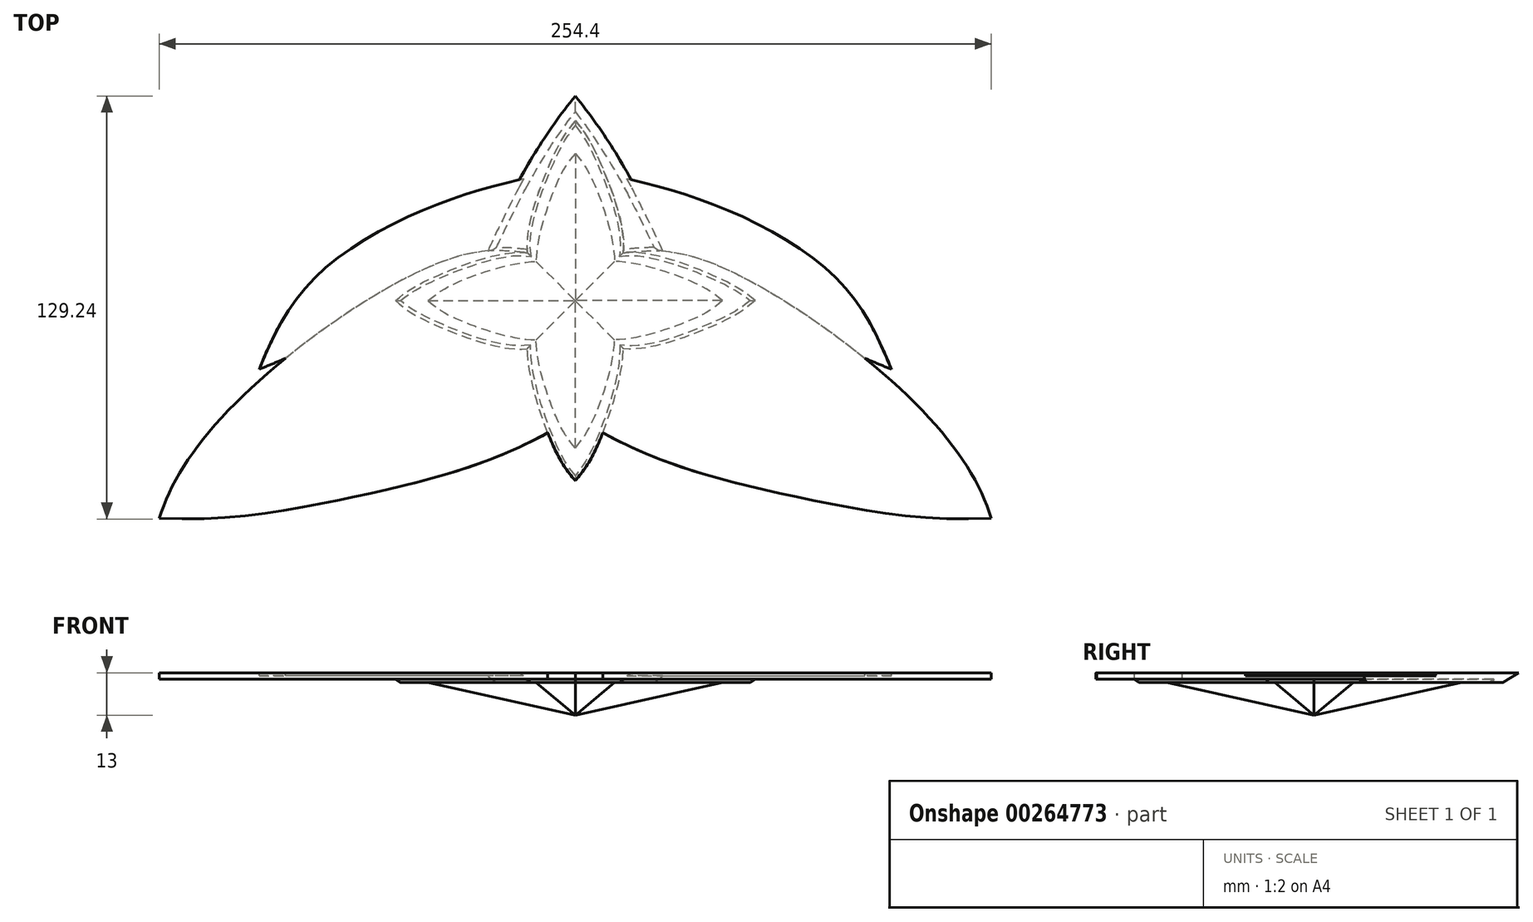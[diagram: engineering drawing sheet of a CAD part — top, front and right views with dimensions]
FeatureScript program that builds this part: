
annotation { "Feature Type Name" : "Feature", "Feature Type Description" : "" }
export const myFeature = defineFeature(function(context is Context, id is Id, definition is map)
    precondition{}
    {
        {
            var Q0;
            Q0=qCreatedBy(makeId("Top.planeOp"),FACE);
            var sketch = newSketch(context, id + "F0", { "sketchPlane" : qUnion([Q0])});
            skLineSegment(sketch, "E0", {"start": v(0, 0) * mm, "end": v(0, 50) * mm});
            skLineSegment(sketch, "E1", {"start": v(0, 0) * mm, "end": v(-50, 0) * mm});
            skFitSpline(sketch, "E2", {"points": [v(0, 50) * mm, v(-50, 0) * mm], "startDerivative": vector(-22.26, -93.04) * mm, "endDerivative": vector(-77.74, -6.96) * mm});
            skFitSpline(sketch, "E3.MirrorCS", {"points": [v(0, 50) * mm, v(50, 0) * mm], "startDerivative": vector(22.26, -93.04) * mm, "endDerivative": vector(77.74, -6.96) * mm});
            skFitSpline(sketch, "E4.MirrorCS", {"points": [v(0, -50) * mm, v(-50, 0) * mm], "startDerivative": vector(-22.26, 93.04) * mm, "endDerivative": vector(-77.74, 6.96) * mm});
            skFitSpline(sketch, "E5.MirrorCS", {"points": [v(0, -50) * mm, v(50, 0) * mm], "startDerivative": vector(22.26, 93.04) * mm, "endDerivative": vector(77.74, 6.96) * mm});
            skSolve(sketch);
        }
        {
            var Q0;
            Q0=qCreatedBy(makeId("Top.planeOp"),FACE);
            var sketch = newSketch(context, id + "F1", { "sketchPlane" : qUnion([Q0])});
            skFitSpline(sketch, "E6", {"points": [v(0, 49.98) * mm, v(-7.34, 30.13) * mm, v(-11.2, 11.2) * mm], "startDerivative": vector(-14.95, -18.4) * mm, "endDerivative": vector(-4.03, -50.51) * mm});
            skFitSpline(sketch, "E7.MirrorCS", {"points": [v(0, 49.98) * mm, v(7.34, 30.13) * mm, v(11.2, 11.2) * mm], "startDerivative": vector(14.95, -18.4) * mm, "endDerivative": vector(4.03, -50.51) * mm});
            skFitSpline(sketch, "E8.MirrorCS", {"points": [v(0, -49.98) * mm, v(-7.34, -30.13) * mm, v(-11.2, -11.2) * mm], "startDerivative": vector(-14.95, 18.4) * mm, "endDerivative": vector(-4.03, 50.51) * mm});
            skFitSpline(sketch, "E9.MirrorCS", {"points": [v(0, -49.98) * mm, v(7.34, -30.13) * mm, v(11.2, -11.2) * mm], "startDerivative": vector(14.95, 18.4) * mm, "endDerivative": vector(4.03, 50.51) * mm});
            skLineSegment(sketch, "E10", {"start": v(-11.2, 11.2) * mm, "end": v(11.2, -11.2) * mm, "construction": true});
            skLineSegment(sketch, "E11", {"start": v(11.2, 11.2) * mm, "end": v(-11.2, -11.2) * mm, "construction": true});
            skFitSpline(sketch, "E12.MirrorCS", {"points": [v(-49.98, 0) * mm, v(-30.13, -7.34) * mm, v(-11.2, -11.2) * mm], "startDerivative": vector(18.4, -14.95) * mm, "endDerivative": vector(50.51, -4.03) * mm});
            skFitSpline(sketch, "E13.MirrorCS", {"points": [v(-49.98, 0) * mm, v(-30.13, 7.34) * mm, v(-11.2, 11.2) * mm], "startDerivative": vector(18.4, 14.95) * mm, "endDerivative": vector(50.51, 4.03) * mm});
            skFitSpline(sketch, "E14.MirrorCS", {"points": [v(49.98, 0) * mm, v(30.13, 7.34) * mm, v(11.2, 11.2) * mm], "startDerivative": vector(-18.4, 14.95) * mm, "endDerivative": vector(-50.51, 4.03) * mm});
            skFitSpline(sketch, "E15.MirrorCS", {"points": [v(49.98, 0) * mm, v(30.13, -7.34) * mm, v(11.2, -11.2) * mm], "startDerivative": vector(-18.4, -14.95) * mm, "endDerivative": vector(-50.51, -4.03) * mm});
            skLineSegment(sketch, "E16", {"start": v(0, 49.98) * mm, "end": v(0, 0) * mm, "construction": true});
            skLineSegment(sketch, "E17", {"start": v(0, 0) * mm, "end": v(0, -49.98) * mm, "construction": true});
            skLineSegment(sketch, "E18", {"start": v(0, 0) * mm, "end": v(49.98, 0) * mm, "construction": true});
            skLineSegment(sketch, "E19", {"start": v(0, 0) * mm, "end": v(-49.98, 0) * mm, "construction": true});
            skSolve(sketch);
        }
        {
            var Q0;
            Q0=qCreatedBy(makeId("Top.planeOp"),FACE);
            cPlane(context, id + "F2", {"entities" : qUnion([Q0]), "cplaneType" : CPlaneType.OFFSET, "offset" : 10 * mm, "width" : 150 * mm, "height" : 150 * mm});
        }
        {
            var Q0;
            Q0=qCreatedBy(id+"F2.planeOp",FACE);
            var sketch = newSketch(context, id + "F3", { "sketchPlane" : qUnion([Q0])});
            skLineSegment(sketch, "E20", {"start": v(0, 0) * mm, "end": v(0, 45) * mm, "construction": true});
            skFitSpline(sketch, "E21", {"points": [v(0, 45) * mm, v(-6.46, 34.06) * mm, v(-11.98, 11.98) * mm], "startDerivative": vector(-19.81, -22.58) * mm, "endDerivative": vector(-0.12, -34.14) * mm});
            skFitSpline(sketch, "E22.MirrorCS", {"points": [v(0, 45) * mm, v(6.46, 34.06) * mm, v(11.98, 11.98) * mm], "startDerivative": vector(19.81, -22.58) * mm, "endDerivative": vector(0.12, -34.14) * mm});
            skFitSpline(sketch, "E23.MirrorCS", {"points": [v(0, -45) * mm, v(-6.46, -34.06) * mm, v(-11.98, -11.98) * mm], "startDerivative": vector(-19.81, 22.58) * mm, "endDerivative": vector(-0.12, 34.14) * mm});
            skFitSpline(sketch, "E24.MirrorCS", {"points": [v(0, -45) * mm, v(6.46, -34.06) * mm, v(11.98, -11.98) * mm], "startDerivative": vector(19.81, 22.58) * mm, "endDerivative": vector(0.12, 34.14) * mm});
            skLineSegment(sketch, "E25", {"start": v(-11.98, 11.98) * mm, "end": v(11.98, -11.98) * mm, "construction": true});
            skLineSegment(sketch, "E26", {"start": v(11.98, 11.98) * mm, "end": v(-11.98, -11.98) * mm, "construction": true});
            skFitSpline(sketch, "E27.MirrorCS", {"points": [v(-45, 0) * mm, v(-34.06, 6.46) * mm, v(-11.98, 11.98) * mm], "startDerivative": vector(22.58, 19.81) * mm, "endDerivative": vector(34.14, 0.12) * mm});
            skFitSpline(sketch, "E28.MirrorCS", {"points": [v(-45, 0) * mm, v(-34.06, -6.46) * mm, v(-11.98, -11.98) * mm], "startDerivative": vector(22.58, -19.81) * mm, "endDerivative": vector(34.14, -0.12) * mm});
            skFitSpline(sketch, "E29.MirrorCS", {"points": [v(45, 0) * mm, v(34.06, -6.46) * mm, v(11.98, -11.98) * mm], "startDerivative": vector(-22.58, -19.81) * mm, "endDerivative": vector(-34.14, -0.12) * mm});
            skFitSpline(sketch, "E30.MirrorCS", {"points": [v(45, 0) * mm, v(34.06, 6.46) * mm, v(11.98, 11.98) * mm], "startDerivative": vector(-22.58, 19.81) * mm, "endDerivative": vector(-34.14, 0.12) * mm});
            skLineSegment(sketch, "E31", {"start": v(0, -45) * mm, "end": v(0, 45) * mm, "construction": true});
            skSolve(sketch);
        }
        {
            var Q0;
            Q0=makeQuery(id+"F3.imprint","IMPRINT",FACE,{"disambiguationData":[TD([[makeQuery(id+"F3.imprint","IMPRINT",EDGE,{"derivedFrom":sQuery(id+"F3.wireOp",EDGE,"E21")}),1.0]])]});
            var Q1;
            Q1=qCreatedBy(makeId("Origin.pointOp"),VERTEX);
            loft(context, id + "F4", {"sheetProfilesArray" : [{ "sheetProfileEntities" : qUnion([Q0]) }, { "sheetProfileEntities" : qUnion([Q1]) }]});
        }
        {
            var Q0;
            Q0=makeQuery(id+"F4.opLoft","CAP_FACE",FACE,{"disambiguationData":[OSD([makeQuery(id+"F3.imprint","IMPRINT",FACE,{"disambiguationData":[TD([[makeQuery(id+"F3.imprint","IMPRINT",EDGE,{"derivedFrom":sQuery(id+"F3.wireOp",EDGE,"E21")}),1.0]])]})])],"isStart":true});
            var sketch = newSketch(context, id + "F5", { "sketchPlane" : qUnion([Q0])});
            skLineSegment(sketch, "E32", {"start": v(0, 0) * mm, "end": v(0, 55) * mm, "construction": true});
            skFitSpline(sketch, "E33", {"points": [v(0, 55) * mm, v(-7.9, 41.63) * mm, v(-14.64, 14.64) * mm], "startDerivative": vector(-24.22, -27.6) * mm, "endDerivative": vector(5.42, -38.74) * mm});
            skFitSpline(sketch, "E34.MirrorCS", {"points": [v(0, 55) * mm, v(7.9, 41.63) * mm, v(14.64, 14.64) * mm], "startDerivative": vector(24.22, -27.6) * mm, "endDerivative": vector(-5.42, -38.74) * mm});
            skFitSpline(sketch, "E35.MirrorCS", {"points": [v(0, -55) * mm, v(-7.9, -41.63) * mm, v(-14.64, -14.64) * mm], "startDerivative": vector(-24.22, 27.6) * mm, "endDerivative": vector(-0.14, 41.73) * mm});
            skFitSpline(sketch, "E36.MirrorCS", {"points": [v(0, -55) * mm, v(7.9, -41.63) * mm, v(14.64, -14.64) * mm], "startDerivative": vector(24.22, 27.6) * mm, "endDerivative": vector(0.14, 41.73) * mm});
            skLineSegment(sketch, "E37", {"start": v(-14.64, 14.64) * mm, "end": v(14.64, -14.64) * mm, "construction": true});
            skLineSegment(sketch, "E38", {"start": v(14.64, 14.64) * mm, "end": v(-14.64, -14.64) * mm, "construction": true});
            skFitSpline(sketch, "E39.MirrorCS", {"points": [v(-55, 0) * mm, v(-41.63, 7.9) * mm, v(-14.64, 14.64) * mm], "startDerivative": vector(27.6, 24.22) * mm, "endDerivative": vector(38.74, -5.42) * mm});
            skFitSpline(sketch, "E40.MirrorCS", {"points": [v(-55, 0) * mm, v(-41.63, -7.9) * mm, v(-14.64, -14.64) * mm], "startDerivative": vector(27.6, -24.22) * mm, "endDerivative": vector(38.74, 5.42) * mm});
            skFitSpline(sketch, "E41.MirrorCS", {"points": [v(55, 0) * mm, v(41.63, -7.9) * mm, v(14.64, -14.64) * mm], "startDerivative": vector(-27.6, -24.22) * mm, "endDerivative": vector(-38.74, 5.42) * mm});
            skFitSpline(sketch, "E42.MirrorCS", {"points": [v(55, 0) * mm, v(41.63, 7.9) * mm, v(14.64, 14.64) * mm], "startDerivative": vector(-27.6, 24.22) * mm, "endDerivative": vector(-38.74, -5.42) * mm});
            skLineSegment(sketch, "E43", {"start": v(0, -55) * mm, "end": v(0, 0) * mm, "construction": true});
            skLineSegment(sketch, "E44", {"start": v(55, 0) * mm, "end": v(0, 0) * mm, "construction": true});
            skLineSegment(sketch, "E45", {"start": v(0, 55) * mm, "end": v(0, 0) * mm, "construction": true});
            skLineSegment(sketch, "E46", {"start": v(0, 0) * mm, "end": v(-55, 0) * mm, "construction": true});
            skSolve(sketch);
        }
        {
            var Q0;
            Q0=makeQuery(id+"F5.imprint","IMPRINT",FACE,{"disambiguationData":[TD([[makeQuery(id+"F5.imprint","IMPRINT",EDGE,{"derivedFrom":sQuery(id+"F5.wireOp",EDGE,"E33")}),1.0]])]});
            var Q1;
            {var subQ2=sQuery(id+"F3.wireOp",EDGE,"E22.MirrorCS");var subQ4=sQuery(id+"F3.wireOp",EDGE,"E27.MirrorCS");var subQ5=sQuery(id+"F3.wireOp",EDGE,"E21");Q1=makeQuery(id+"F5.imprint","IMPRINT",FACE,{"disambiguationData":[TD([[makeQuery(id+"F5.imprint","IMPRINT",EDGE,{"derivedFrom":makeQuery(id+"F4.opLoft","MID_CAP_EDGE",EDGE,{"disambiguationData":[OSD([subQ5,subQ2,subQ4])],"capPos":0.0})}),1.0]])]});}
            extrude(context, id + "F6", {"entities" : qUnion([Q0, Q1]), "operationType" : NewBodyOperationType.ADD, "depth" : 3 * mm, "offsetDistance" : 25 * mm});
        }
        {
            var Q0;
            Q0=makeQuery(id+"F6.opExtrude","CAP_EDGE",EDGE,{"disambiguationData":[OSD([sQuery(id+"F5.wireOp",EDGE,"E35.MirrorCS")])],"isStart":true});
            var Q1;
            Q1=makeQuery(id+"F6.opExtrude","CAP_EDGE",EDGE,{"disambiguationData":[OSD([sQuery(id+"F5.wireOp",EDGE,"E36.MirrorCS")])],"isStart":true});
            var Q2;
            Q2=makeQuery(id+"F6.opExtrude","CAP_EDGE",EDGE,{"disambiguationData":[OSD([sQuery(id+"F5.wireOp",EDGE,"E40.MirrorCS")])],"isStart":true});
            var Q3;
            Q3=makeQuery(id+"F6.opExtrude","CAP_EDGE",EDGE,{"disambiguationData":[OSD([sQuery(id+"F5.wireOp",EDGE,"E39.MirrorCS")])],"isStart":true});
            var Q4;
            Q4=makeQuery(id+"F6.opExtrude","CAP_EDGE",EDGE,{"disambiguationData":[OSD([sQuery(id+"F5.wireOp",EDGE,"E33")])],"isStart":true});
            var Q5;
            Q5=makeQuery(id+"F6.opExtrude","CAP_EDGE",EDGE,{"disambiguationData":[OSD([sQuery(id+"F5.wireOp",EDGE,"E34.MirrorCS")])],"isStart":true});
            var Q6;
            Q6=makeQuery(id+"F6.opExtrude","CAP_EDGE",EDGE,{"disambiguationData":[OSD([sQuery(id+"F5.wireOp",EDGE,"E42.MirrorCS")])],"isStart":true});
            var Q7;
            Q7=makeQuery(id+"F6.opExtrude","CAP_EDGE",EDGE,{"disambiguationData":[OSD([sQuery(id+"F5.wireOp",EDGE,"E41.MirrorCS")])],"isStart":true});
            chamfer(context, id + "F7", {"entities" : qUnion([Q0, Q1, Q2, Q3, Q4, Q5, Q6, Q7]), "width" : 1 * mm, "tangentPropagation" : true});
        }
        {
            var Q0;
            Q0=makeQuery(id+"F6.opExtrude","CAP_FACE",FACE,{"disambiguationData":[OSD([sQuery(id+"F5.wireOp",EDGE,"E33"),sQuery(id+"F5.wireOp",EDGE,"E34.MirrorCS"),sQuery(id+"F5.wireOp",EDGE,"E35.MirrorCS"),sQuery(id+"F5.wireOp",EDGE,"E36.MirrorCS"),sQuery(id+"F5.wireOp",EDGE,"E39.MirrorCS"),sQuery(id+"F5.wireOp",EDGE,"E40.MirrorCS"),sQuery(id+"F5.wireOp",EDGE,"E41.MirrorCS"),sQuery(id+"F5.wireOp",EDGE,"E42.MirrorCS")])],"isStart":false});
            var sketch = newSketch(context, id + "F8", { "sketchPlane" : qUnion([Q0])});
            skFitSpline(sketch, "E47", {"points": [v(8.4, -40.37) * mm, v(38.63, -52.8) * mm, v(73.35, -61.15) * mm, v(127.2, -66.45) * mm], "startDerivative": vector(101.37, -54.96) * mm, "endDerivative": vector(163.5, 9.13) * mm});
            skFitSpline(sketch, "E48", {"points": [v(14.64, 14.64) * mm, v(38.6, 12.68) * mm, v(102.88, -30.26) * mm, v(127.2, -66.45) * mm], "startDerivative": vector(85.37, 9.14) * mm, "endDerivative": vector(31.49, -101.03) * mm});
            skFitSpline(sketch, "E49", {"points": [v(9.14, 38.67) * mm, v(42.23, 29.41) * mm, v(80.3, 6.36) * mm, v(96.65, -20.99) * mm], "startDerivative": vector(93.7, -19.67) * mm, "endDerivative": vector(36.32, -89.57) * mm});
            skFitSpline(sketch, "E50", {"points": [v(96.65, -20.99) * mm, v(88.57, -17.6) * mm], "startDerivative": vector(-8.1, 3.36) * mm, "endDerivative": vector(-8.1, 3.36) * mm});
            skFitSpline(sketch, "E51.MirrorCS", {"points": [v(-8.4, -40.37) * mm, v(-38.63, -52.8) * mm, v(-73.35, -61.15) * mm, v(-127.2, -66.45) * mm], "startDerivative": vector(-101.37, -54.96) * mm, "endDerivative": vector(-163.5, 9.13) * mm});
            skFitSpline(sketch, "E52.MirrorCS", {"points": [v(-14.64, 14.64) * mm, v(-38.6, 12.68) * mm, v(-102.88, -30.26) * mm, v(-127.2, -66.45) * mm], "startDerivative": vector(-85.37, 9.14) * mm, "endDerivative": vector(-31.49, -101.03) * mm});
            skFitSpline(sketch, "E53.MirrorCS", {"points": [v(-9.14, 38.67) * mm, v(-42.23, 29.41) * mm, v(-80.3, 6.36) * mm, v(-96.65, -20.99) * mm], "startDerivative": vector(-93.7, -19.67) * mm, "endDerivative": vector(-36.32, -89.57) * mm});
            skFitSpline(sketch, "E54.MirrorCS", {"points": [v(-96.65, -20.99) * mm, v(-88.57, -17.6) * mm], "startDerivative": vector(8.1, 3.36) * mm, "endDerivative": vector(8.1, 3.36) * mm});
            skFitSpline(sketch, "E55", {"points": [v(-31.44, 11.84) * mm, v(-25.1, 25.7) * mm, v(0, 65.66) * mm], "startDerivative": vector(13.55, 33.83) * mm, "endDerivative": vector(59.2, 69.46) * mm});
            skFitSpline(sketch, "E56.MirrorCS", {"points": [v(31.44, 11.84) * mm, v(25.1, 25.7) * mm, v(0, 65.66) * mm], "startDerivative": vector(-13.55, 33.83) * mm, "endDerivative": vector(-59.2, 69.46) * mm});
            skSolve(sketch);
        }
        {
            var Q0;
            {var subQ4=sQuery(id+"F8.wireOp",EDGE,"E51.MirrorCS");Q0=makeQuery(id+"F8.imprint","IMPRINT",FACE,{"disambiguationData":[TD([[makeQuery(id+"F8.imprint","IMPRINT",EDGE,{"derivedFrom":subQ4}),-1.0]])]});}
            var Q1;
            {var subQ5=sQuery(id+"F8.wireOp",EDGE,"E47");Q1=makeQuery(id+"F8.imprint","IMPRINT",FACE,{"disambiguationData":[TD([[makeQuery(id+"F8.imprint","IMPRINT",EDGE,{"derivedFrom":subQ5}),1.0]])]});}
            var Q2;
            {var subQ0=sQuery(id+"F8.wireOp",EDGE,"E55");var subQ1=sQuery(id+"F8.wireOp",EDGE,"E52.MirrorCS");var subQ2=makeQuery(id+"F8.imprint","INTERSECT",VERTEX,{"derivedFrom":[subQ1,subQ0]});Q2=makeQuery(id+"F8.imprint","IMPRINT",FACE,{"disambiguationData":[TD([[makeQuery(id+"F8.imprint","IMPRINT",EDGE,{"disambiguationData":[TD([[subQ2,1.0]])],"derivedFrom":subQ1}),1.0]])]});}
            var Q3;
            {var subQ0=sQuery(id+"F8.wireOp",EDGE,"E56.MirrorCS");var subQ1=sQuery(id+"F8.wireOp",EDGE,"E48");var subQ2=makeQuery(id+"F8.imprint","INTERSECT",VERTEX,{"derivedFrom":[subQ1,subQ0]});Q3=makeQuery(id+"F8.imprint","IMPRINT",FACE,{"disambiguationData":[TD([[makeQuery(id+"F8.imprint","IMPRINT",EDGE,{"disambiguationData":[TD([[subQ2,1.0]])],"derivedFrom":subQ1}),-1.0]])]});}
            extrude(context, id + "F9", {"entities" : qUnion([Q0, Q1, Q2, Q3]), "operationType" : NewBodyOperationType.ADD, "oppositeDirection" : true, "depth" : 2 * mm, "offsetDistance" : 25 * mm});
        }
        {
            var Q0;
            {var subQ6=sQuery(id+"F8.wireOp",EDGE,"E53.MirrorCS");Q0=makeQuery(id+"F8.imprint","IMPRINT",FACE,{"disambiguationData":[TD([[makeQuery(id+"F8.imprint","IMPRINT",EDGE,{"derivedFrom":subQ6}),1.0]])]});}
            var Q1;
            {var subQ1=sQuery(id+"F8.wireOp",EDGE,"E49");Q1=makeQuery(id+"F8.imprint","IMPRINT",FACE,{"disambiguationData":[TD([[makeQuery(id+"F8.imprint","IMPRINT",EDGE,{"derivedFrom":subQ1}),-1.0]])]});}
            var Q2;
            {var subQ0=sQuery(id+"F8.wireOp",EDGE,"E55");var subQ3=sQuery(id+"F8.wireOp",EDGE,"E52.MirrorCS");var subQ4=makeQuery(id+"F8.imprint","INTERSECT",VERTEX,{"derivedFrom":[subQ3,subQ0]});Q2=makeQuery(id+"F8.imprint","IMPRINT",FACE,{"disambiguationData":[TD([[makeQuery(id+"F8.imprint","IMPRINT",EDGE,{"disambiguationData":[TD([[subQ4,1.0]])],"derivedFrom":subQ3}),-1.0]])]});}
            var Q3;
            {var subQ0=sQuery(id+"F8.wireOp",EDGE,"E56.MirrorCS");var subQ3=sQuery(id+"F8.wireOp",EDGE,"E48");var subQ4=makeQuery(id+"F8.imprint","INTERSECT",VERTEX,{"derivedFrom":[subQ3,subQ0]});Q3=makeQuery(id+"F8.imprint","IMPRINT",FACE,{"disambiguationData":[TD([[makeQuery(id+"F8.imprint","IMPRINT",EDGE,{"disambiguationData":[TD([[subQ4,1.0]])],"derivedFrom":subQ3}),1.0]])]});}
            extrude(context, id + "F10", {"entities" : qUnion([Q0, Q1, Q2, Q3]), "operationType" : NewBodyOperationType.ADD, "oppositeDirection" : true, "depth" : 1 * mm, "offsetDistance" : 25 * mm});
        }
        {
            var Q0;
            {var subQ3=sQuery(id+"F8.wireOp",EDGE,"E49");var subQ9=makeQuery(id+"F6.opExtrude","CAP_EDGE",EDGE,{"disambiguationData":[OSD([sQuery(id+"F5.wireOp",EDGE,"E34.MirrorCS")])],"isStart":false});var subQ11=makeQuery(id+"F8.imprint","INTERSECT",VERTEX,{"derivedFrom":[subQ9,subQ3]});Q0=makeQuery(id+"F8.imprint","IMPRINT",FACE,{"disambiguationData":[TD([[makeQuery(id+"F8.imprint","IMPRINT",EDGE,{"disambiguationData":[TD([[subQ11,-1.0]])],"derivedFrom":subQ3}),1.0]])]});}
            var Q1;
            {var subQ0=sQuery(id+"F8.wireOp",EDGE,"E55");var subQ3=sQuery(id+"F8.wireOp",EDGE,"E52.MirrorCS");var subQ4=makeQuery(id+"F8.imprint","INTERSECT",VERTEX,{"derivedFrom":[subQ3,subQ0]});Q1=makeQuery(id+"F8.imprint","IMPRINT",FACE,{"disambiguationData":[TD([[makeQuery(id+"F8.imprint","IMPRINT",EDGE,{"disambiguationData":[TD([[subQ4,1.0]])],"derivedFrom":subQ3}),-1.0]])]});}
            var Q2;
            {var subQ0=sQuery(id+"F8.wireOp",EDGE,"E56.MirrorCS");var subQ3=sQuery(id+"F8.wireOp",EDGE,"E48");var subQ4=makeQuery(id+"F8.imprint","INTERSECT",VERTEX,{"derivedFrom":[subQ3,subQ0]});Q2=makeQuery(id+"F8.imprint","IMPRINT",FACE,{"disambiguationData":[TD([[makeQuery(id+"F8.imprint","IMPRINT",EDGE,{"disambiguationData":[TD([[subQ4,1.0]])],"derivedFrom":subQ3}),1.0]])]});}
            extrude(context, id + "F11", {"entities" : qUnion([Q0, Q1, Q2]), "operationType" : NewBodyOperationType.ADD, "oppositeDirection" : true, "depth" : 3 * mm, "offsetDistance" : 25 * mm});
        }
        {
            var Q0;
            Q0=makeQuery(id+"F11.opExtrude","CAP_EDGE",EDGE,{"disambiguationData":[OSD([sQuery(id+"F8.wireOp",EDGE,"E55")])],"isStart":false});
            var Q1;
            Q1=makeQuery(id+"F11.opExtrude","CAP_EDGE",EDGE,{"disambiguationData":[OSD([sQuery(id+"F8.wireOp",EDGE,"E56.MirrorCS")])],"isStart":false});
            chamfer(context, id + "F12", {"entities" : qUnion([Q0, Q1]), "width" : 5 * mm, "tangentPropagation" : true});
        }
        {
            var Q0;
            Q0=makeQuery(id+"F11.opExtrude","CAP_EDGE",EDGE,{"disambiguationData":[OSD([sQuery(id+"F8.wireOp",EDGE,"E52.MirrorCS")])],"isStart":false});
            var Q1;
            Q1=makeQuery(id+"F11.opExtrude","CAP_EDGE",EDGE,{"disambiguationData":[OSD([sQuery(id+"F8.wireOp",EDGE,"E48")])],"isStart":false});
            chamfer(context, id + "F13", {"entities" : qUnion([Q0, Q1]), "width" : 1 * mm, "tangentPropagation" : true});
        }
    });
